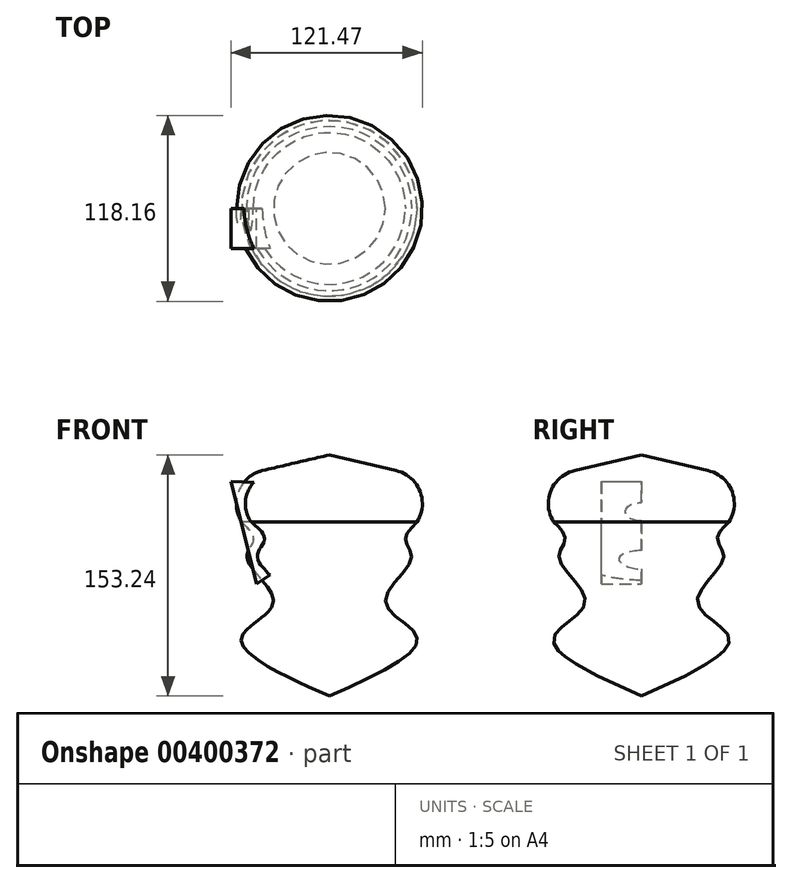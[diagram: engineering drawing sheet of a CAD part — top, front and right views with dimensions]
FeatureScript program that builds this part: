
annotation { "Feature Type Name" : "Feature", "Feature Type Description" : "" }
export const myFeature = defineFeature(function(context is Context, id is Id, definition is map)
    precondition{}
    {
        {
            var Q0;
            Q0=qCreatedBy(makeId("Front.planeOp"),FACE);
            var sketch = newSketch(context, id + "F0", { "sketchPlane" : qUnion([Q0])});
            skLineSegment(sketch, "E0", {"start": v(0, 76.74) * mm, "end": v(0, -76.5) * mm});
            skLineSegment(sketch, "E1", {"start": v(0, 76.74) * mm, "end": v(42.3, 66.85) * mm});
            skArc(sketch, "E2", {"start": v(55.7, 34.05) * mm, "mid": v(57.46, 53.9) * mm, "end": v(42.3, 66.85) * mm});
            skFitSpline(sketch, "E3", {"points": [v(55.7, 34.05) * mm, v(48.3, 22.75) * mm, v(52.17, 10.83) * mm, v(35.6, -16.86) * mm, v(55.7, -39.01) * mm, v(0, -76.5) * mm], "startDerivative": vector(-85.11, -82.2) * mm, "endDerivative": vector(-286.93, -128.82) * mm});
            skSolve(sketch);
        }
        {
            var Q0;
            Q0=makeQuery(id+"F0.imprint","IMPRINT",FACE,{"disambiguationData":[TD([[makeQuery(id+"F0.imprint","IMPRINT",EDGE,{"derivedFrom":sQuery(id+"F0.wireOp",EDGE,"E0")}),1.0]])]});
            var Q1;
            Q1=sQuery(id+"F0.wireOp",EDGE,"E0");
            revolve(context, id + "F1", {"entities" : qUnion([Q0]), "axis" : qUnion([Q1]), "revolveType" : RevolveType.FULL});
        }
        {
            var Q0;
            Q0=qCreatedBy(makeId("Front.planeOp"),FACE);
            var sketch = newSketch(context, id + "F2", { "sketchPlane" : qUnion([Q0])});
            skLineSegment(sketch, "E4", {"start": v(-62.4, 59.9) * mm, "end": v(48.3, 55.89) * mm});
            skLineSegment(sketch, "E5", {"start": v(48.3, 55.89) * mm, "end": v(-46.18, -5.22) * mm});
            skLineSegment(sketch, "E6", {"start": v(-46.18, -5.22) * mm, "end": v(-62.4, 59.9) * mm});
            skSolve(sketch);
        }
        {
            var Q0;
            Q0 = qSketchRegion(id + "F2", true);
            extrude(context, id + "F3", {"entities" : qUnion([Q0]), "operationType" : NewBodyOperationType.ADD, "depth" : 25.4 * mm});
        }
    });
